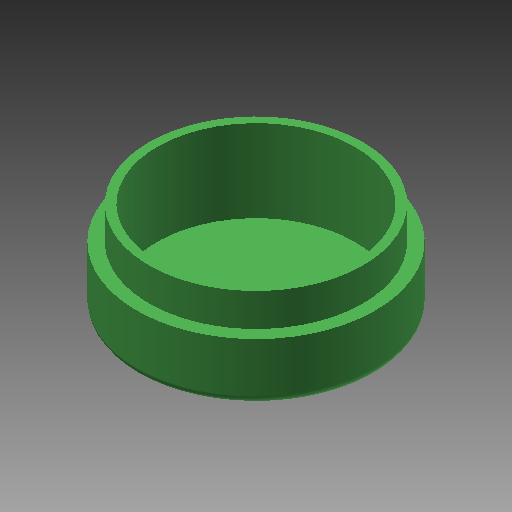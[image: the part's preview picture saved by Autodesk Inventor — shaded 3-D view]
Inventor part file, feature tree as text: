
AUTODESK INVENTOR PART (.ipt)
format: ipt  version: 2017 (Build 210142000, 142)  size: 109,056 bytes
history: native  units: in
note: dims shown in document units (in); Inventor stores cm internally (conversion verified against a paired STEP export)
features: fillet x1, other x1, imported_body x1
ambient origin geometry x8: Origin, YZ Plane, XZ Plane, XY Plane, X Axis, Y Axis, Z Axis, Center Point
bodies: Body1 (feature_tree)
feature tree (3):
  fillet  "Fillet1"  [1 undecoded]
  other  "light green.ipt1"
  imported_body  "Base1"
note: 1 required parameter value undecoded (feature->parameter linkage not recoverable at this tier; creation-order binding heuristic only, values carry confidence <= 0.55)
